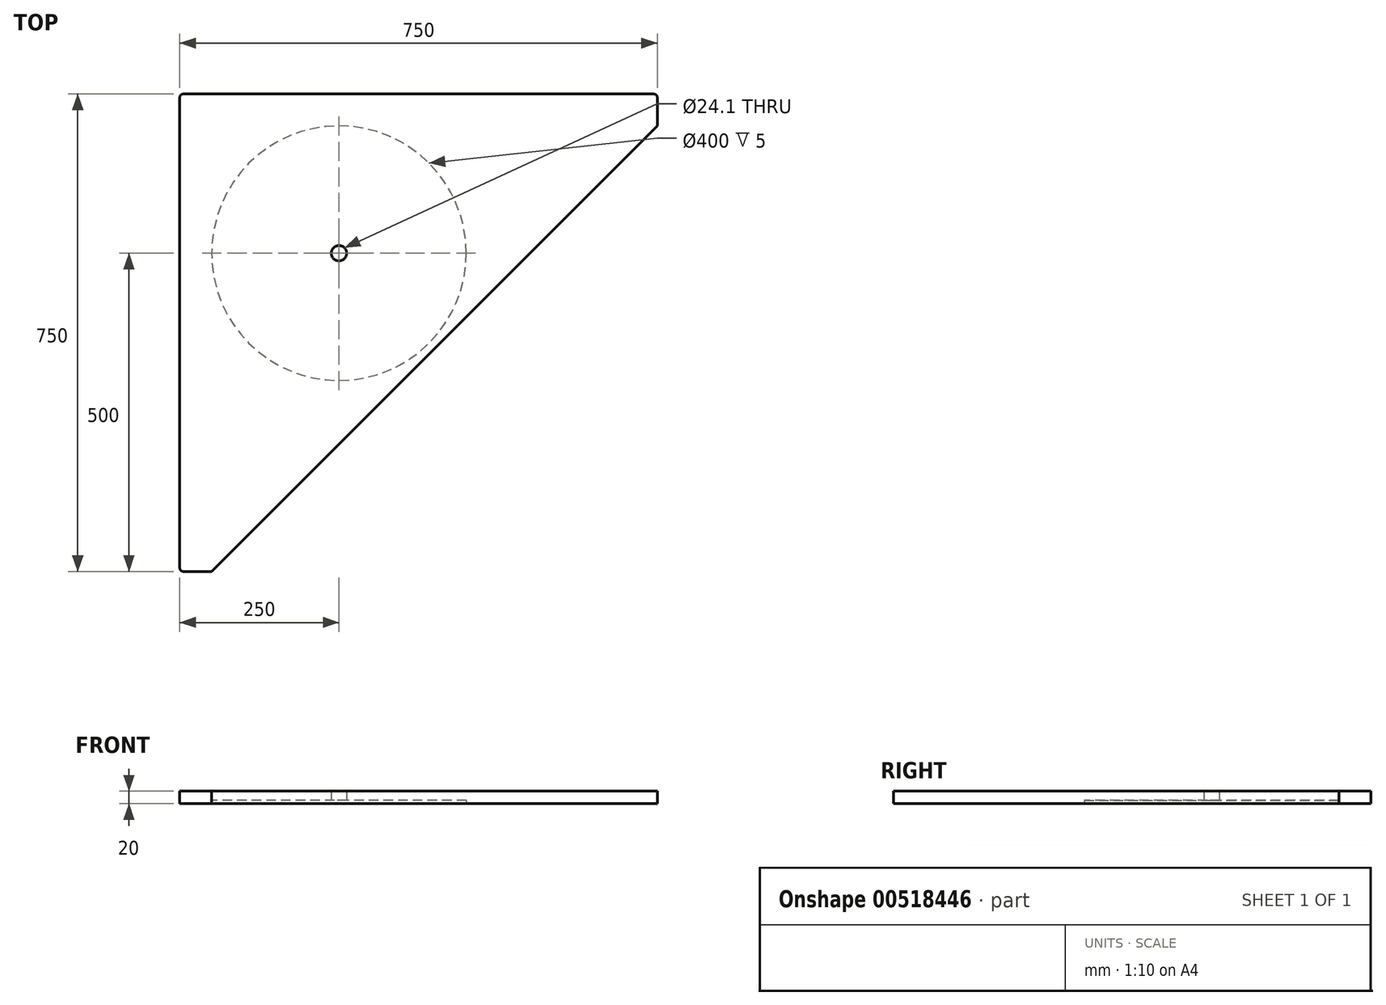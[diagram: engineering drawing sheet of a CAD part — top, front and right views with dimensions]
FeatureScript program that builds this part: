
annotation { "Feature Type Name" : "Feature", "Feature Type Description" : "" }
export const myFeature = defineFeature(function(context is Context, id is Id, definition is map)
    precondition{}
    {
        {
            var Q0;
            Q0=qCreatedBy(makeId("Top.planeOp"),FACE);
            var sketch = newSketch(context, id + "F0", { "sketchPlane" : qUnion([Q0])});
            skLineSegment(sketch, "E0", {"start": v(0, 0) * mm, "end": v(750, 0) * mm});
            skLineSegment(sketch, "E1", {"start": v(0, -750) * mm, "end": v(0, 0) * mm});
            skCircle(sketch, "E2", {"center": v(250, -250) * mm, "radius": 12.05 * mm});
            skLineSegment(sketch, "E3", {"start": v(750, 0) * mm, "end": v(750, -50) * mm});
            skLineSegment(sketch, "E4", {"start": v(750, -50) * mm, "end": v(50, -750) * mm});
            skLineSegment(sketch, "E5", {"start": v(50, -750) * mm, "end": v(0, -750) * mm});
            skSolve(sketch);
        }
        {
            var Q0;
            Q0=makeQuery(id+"F0.imprint","IMPRINT",FACE,{"disambiguationData":[TD([[makeQuery(id+"F0.imprint","IMPRINT",EDGE,{"derivedFrom":sQuery(id+"F0.wireOp",EDGE,"E0")}),-1.0]])]});
            extrude(context, id + "F1", {"entities" : qUnion([Q0]), "depth" : 20 * mm, "offsetDistance" : 25 * mm});
        }
        {
            var Q0;
            Q0=makeQuery(id+"F1.opExtrude","SWEPT_EDGE",EDGE,{"disambiguationData":[OSD([sQuery(id+"F0.wireOp",EDGE,"E1"),sQuery(id+"F0.wireOp",EDGE,"E5")])]});
            var Q1;
            Q1=makeQuery(id+"F1.opExtrude","SWEPT_EDGE",EDGE,{"disambiguationData":[OSD([sQuery(id+"F0.wireOp",EDGE,"E0"),sQuery(id+"F0.wireOp",EDGE,"E3")])]});
            var Q2;
            Q2=makeQuery(id+"F1.opExtrude","SWEPT_EDGE",EDGE,{"disambiguationData":[OSD([sQuery(id+"F0.wireOp",EDGE,"E0"),sQuery(id+"F0.wireOp",EDGE,"E1")])]});
            fillet(context, id + "F2", {"entities" : qUnion([Q0, Q1, Q2]), "radius" : 5 * mm, "tangentPropagation" : true, "allowEdgeOverflow" : false});
        }
        {
            var Q0;
            Q0=qCreatedBy(makeId("Top.planeOp"),FACE);
            var sketch = newSketch(context, id + "F3", { "sketchPlane" : qUnion([Q0])});
            skCircle(sketch, "E6", {"center": v(250, -250) * mm, "radius": 200 * mm});
            skSolve(sketch);
        }
        {
            var Q0;
            Q0 = qSketchRegion(id + "F3", true);
            extrude(context, id + "F4", {"entities" : qUnion([Q0]), "operationType" : NewBodyOperationType.REMOVE, "depth" : 5 * mm, "offsetDistance" : 25 * mm});
        }
    });
